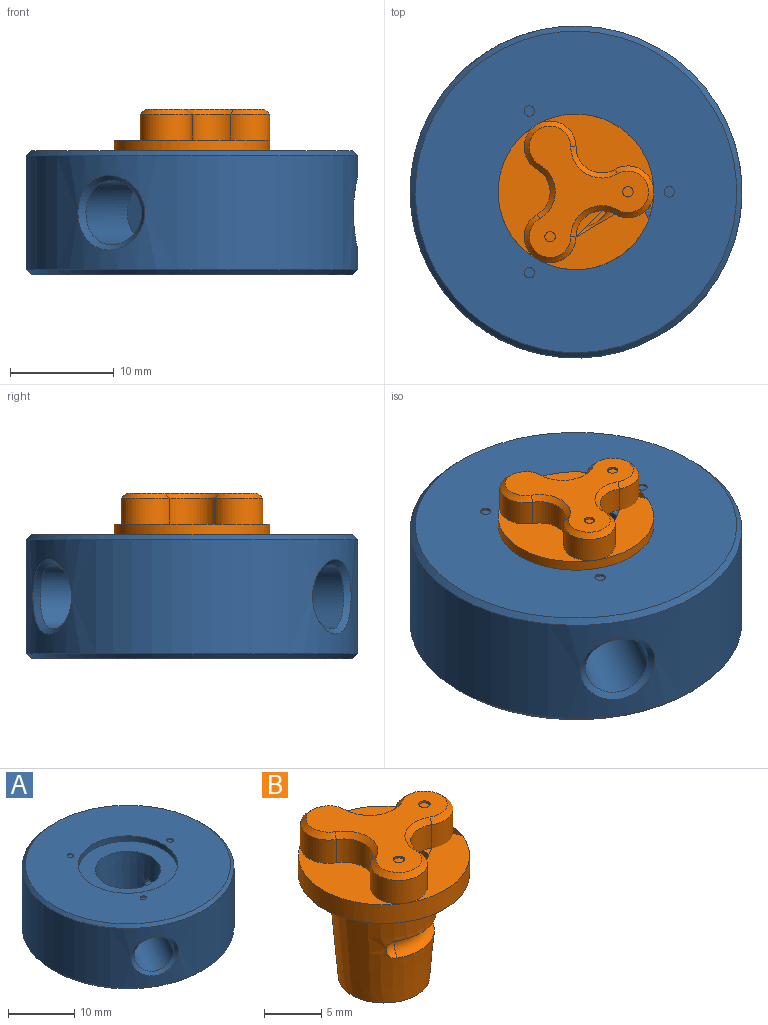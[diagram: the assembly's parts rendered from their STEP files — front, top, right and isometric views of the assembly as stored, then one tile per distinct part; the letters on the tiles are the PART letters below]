
ASSEMBLY  parts=2 mates=1
PART A: 32 faces, bbox 32x32x12 mm
  f0: cone r=5mm half-angle=4.8deg, axis (0,0,1), area 303.5mm2, adj f2,f4,f5,f6,f9,f10,f11,f14
  f1: plane 31x31mm, normal (0,0,1), area 575.7mm2, adj f23,f24,f26,f28,f30
  f2: plane 31x31mm, normal (0,0,-1), area 704.5mm2, adj f0,f22
  f3: cylinder r=16mm len=32mm, axis (0,0,-1), area 979.1mm2, adj f19,f20,f21,f22,f23
  f4: sphere r=0.8mm, area 0mm2, adj f0,f6
  f5: sphere r=0.8mm, area 0mm2, adj f0,f6
  f6: cylinder r=0.8mm len=3.11mm, axis (-0.5,-0.87,0), area 13.4mm2, adj f0,f4,f5,f7
  f7: plane 6.2x5.37mm, normal (-0.5,-0.87,0), area 28.2mm2, adj f6,f8
  f8: cylinder r=3.1mm len=10.37mm, axis (-0.5,-0.87,0), area 163.6mm2, adj f7,f20
  f9: sphere r=0.8mm, area 0mm2, adj f0,f11
  f10: sphere r=0.8mm, area 0mm2, adj f0,f11
  f11: cylinder r=0.8mm len=3.11mm, axis (-0.5,0.87,0), area 13.4mm2, adj f0,f9,f10,f12
  f12: plane 6.2x5.37mm, normal (-0.5,0.87,0), area 28.2mm2, adj f11,f13
  f13: cylinder r=3.1mm len=10.37mm, axis (-0.5,0.87,0), area 163.6mm2, adj f12,f19
  f14: sphere r=0.8mm, area 0mm2, adj f0,f16
  f15: sphere r=0.8mm, area 0mm2, adj f0,f16
  f16: cylinder r=0.8mm len=2.67mm, axis (1,0,0), area 13.2mm2, adj f0,f14,f15,f17
  f17: plane 6.2x6.2mm, normal (1,0,0), area 28.2mm2, adj f16,f18
  f18: cylinder r=3.1mm len=8.4mm, axis (1,0,0), area 163.6mm2, adj f17,f21
  f19: bspline ~7.2x6.44mm, area 15.9mm2, adj f3,f13
  f20: bspline ~7.2x6.44mm, area 15.9mm2, adj f3,f8
  f21: bspline ~7.43x7.2mm, area 15.9mm2, adj f3,f18
  f22: cone r=15.5mm half-angle=45deg, axis (0,0,1), area 70mm2, adj f2,f3
  f23: cone r=16mm half-angle=45deg, axis (0,0,-1), area 70mm2, adj f1,f3
  f24: cylinder r=0.5mm len=1mm, axis (0,0,1), area 0.6mm2, adj f1,f25
  f25: plane 1x1mm, normal (0,0,1), area 0.8mm2, adj f24
  f26: cylinder r=0.5mm len=1mm, axis (0,0,1), area 0.6mm2, adj f1,f27
  f27: plane 1x1mm, normal (0,0,1), area 0.8mm2, adj f26
  f28: cylinder r=0.5mm len=1mm, axis (0,0,1), area 0.6mm2, adj f1,f29
  f29: plane 1x1mm, normal (0,0,1), area 0.8mm2, adj f28
  f30: cylinder r=7.5mm len=15mm, axis (0,0,-1), area 47.1mm2, adj f1,f31
  f31: plane 15x15mm, normal (0,0,1), area 100.8mm2, adj f0,f30
PART B: 27 faces, bbox 15x15x16 mm
  f0: plane 12.99x5mm, normal (0,0,1), area 30.7mm2, adj f7,f13,f14,f15
  f1: plane 11.25x7.5mm, normal (0,0,1), area 30.7mm2, adj f7,f10,f11,f15
  f2: cone r=5mm half-angle=4.8deg, axis (0,0,1), area 287.2mm2, adj f3,f4,f5,f6,f9
  f3: plane 8x8mm, normal (0,0,-1), area 50.3mm2, adj f2
  f4: torus R=4.5mm, axis (0,0,-1), area 25.4mm2, adj f2,f5,f6
  f5: sphere r=1mm, area 3mm2, adj f2,f4
  f6: sphere r=1mm, area 3mm2, adj f2,f4
  f7: cylinder r=7.5mm len=15mm, axis (0,0,-1), area 94.2mm2, adj f0,f1,f8,f9
  f8: plane 11.25x7.5mm, normal (0,0,1), area 30.7mm2, adj f7,f11,f12,f13
  f9: plane 15x15mm, normal (0,0,-1), area 100.8mm2, adj f2,f7
  f10: cylinder r=2.5mm len=3.75mm, axis (0,0,-1), area 13.1mm2, adj f1,f11,f15,f18
  f11: cylinder r=2.5mm len=5mm, axis (0,0,-1), area 26.2mm2, adj f1,f8,f10,f12,f17
  f12: cylinder r=2.5mm len=3.75mm, axis (0,0,-1), area 13.1mm2, adj f8,f11,f13,f19
  f13: cylinder r=2.5mm len=5mm, axis (0,0,-1), area 26.2mm2, adj f0,f8,f12,f14,f21
  f14: cylinder r=2.5mm len=4.33mm, axis (0,0,-1), area 13.1mm2, adj f0,f13,f15,f22
  f15: cylinder r=2.5mm len=5mm, axis (0,0,-1), area 26.2mm2, adj f0,f1,f10,f14,f20
  f16: plane 12.66x11.5mm, normal (0,0,1), area 60.2mm2, adj f17,f18,f19,f20,f21,f22,f23,f25
  f17: cone r=2mm half-angle=45deg, axis (0,0,-1), area 6.7mm2, adj f11,f16,f18,f19
  f18: cone r=2.5mm half-angle=45deg, axis (0,0,1), area 4.1mm2, adj f10,f16,f17,f20
  f19: cone r=2.5mm half-angle=45deg, axis (0,0,1), area 4.1mm2, adj f12,f16,f17,f21
  f20: cone r=2mm half-angle=45deg, axis (0,0,-1), area 6.7mm2, adj f15,f16,f18,f22
  f21: cone r=2mm half-angle=45deg, axis (0,0,-1), area 6.7mm2, adj f13,f16,f19,f22
  f22: cone r=2.5mm half-angle=45deg, axis (0,0,1), area 4.1mm2, adj f14,f16,f20,f21
  f23: cylinder r=0.5mm len=1mm, axis (0,0,1), area 0.6mm2, adj f16,f24
  f24: plane 1x1mm, normal (0,0,1), area 0.8mm2, adj f23
  f25: cylinder r=0.5mm len=1mm, axis (0,0,1), area 0.6mm2, adj f16,f26
  f26: plane 1x1mm, normal (0,0,1), area 0.8mm2, adj f25
PLACE A at identity
PLACE B at identity
MATE revolute B.f2 <-> A.f0  axis (0,0,-1) through (0,0,0)mm
